# Revit family: Deca_Assento poliéster com protekto_Monte Carlo_AP.81
name_source: partatom
category: Plumbing Fixtures
units: mm (PartAtom-declared; Revit-internal decimal feet)

## family parameters
Cut with Voids When Loaded = No
Host = Face
Part Type = Normal
Room Calculation Point = No
Round Connector Dimension = Use Diameter
Shared = No

## types (3) — shared parameters
Acompanha o Produto = FIXAÇÃO ASSENTO  (FERRAGEM C/AMORTECEDOR )
Aprovado por = quattroD
Atendimento ao Cliente = 0800-0117073
Categoria = ASSENTOS
Composição Anel Vedação = -
Composição Assento = -
Composição Básica = Resina Poliéster
Composição Componente = Não Possui
Consumo = -
Cor Interna = -
Cor Secundária = -
Cores Componente = Cromado
Criado por = quattroD
Código Pai = AP.81
Description = Assento poliéster com Protekto
Informações Complementares = -
Itens de Instalação = -
Linha = Assento Poliéster Médio
Manufacturer = Deca
Material Secundário = Deca_Ligas de Cobre (Bronze e Latão)
Norma = NBR-16729
Peso Líquido (Kg) = 3.8
Pressão máx. funcionamento = -
Pressão mín. Aquec. Acúmulo = -
Pressão mín. Aquec. Passagem = -
Pressão mín. funcionamento = -
Saída de Esgoto = -
Segmento = Banheiro Médio
Tipo de dispositivo economizador = -
Tipo de mecanismo utilizado = -
Tipo de rosca de entrada = -
Tipo de rosca de saída = -
URL = www.deca.com.br
Vazão na Pressão máx. (L/min) = -
Vazão na Pressão mín. (L/min) = -
zero-valued in all types: Default Elevation

## per-type parameters (varying)
| type | Cor Principal | Material | Model |
| AP.81.17_Branco | Branco | Deca_Plástico - Branco | AP.81.17 |
| AP.81.37_Creme | Creme | Deca_Plástico - Creme | AP.81.37 |
| AP.81.95_Ébano | Ébano | Deca_Plástico - Ébano | AP.81.95 |

## geometry (parser evidence)
native form markers: Sweep x1
no freeform markers — native parametric forms only
